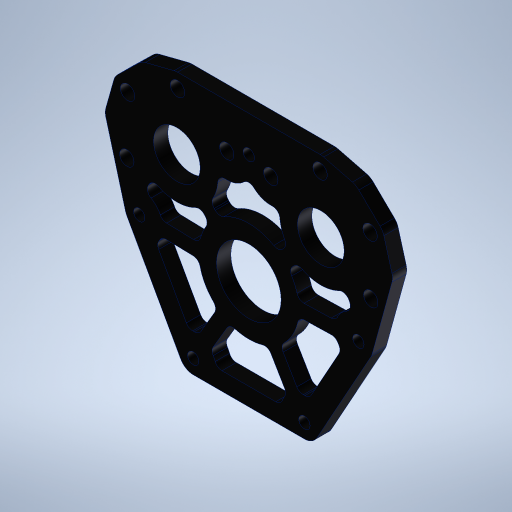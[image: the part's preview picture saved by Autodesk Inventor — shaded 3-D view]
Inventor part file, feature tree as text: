
AUTODESK INVENTOR PART (.ipt)
format: ipt  version: 2024 (Build 280153000, 153)  size: 578,560 bytes
history: native  units: in
note: dims shown in document units (in); Inventor stores cm internally (conversion verified against a paired STEP export)
features: fillet x6, extrude x2, sketch x2, projected_geometry x1
ambient origin geometry x8: Origin, YZ Plane, XZ Plane, XY Plane, X Axis, Y Axis, Z Axis, Center Point
bodies: Solid1 (feature_tree)
feature tree (11):
  extrude  "Extrusion1"  Depth=0.1in
  extrude  "Extrusion2"  Depth=0.125in
  fillet  "Fillet1"  Radius=2.0in
  fillet  "Fillet2"  Radius=0.6in
  fillet  "Fillet3"  Radius=0.25in
  fillet  "Fillet4"  Radius=4.7244in
  fillet  "Fillet5"  Radius=0.5in
  fillet  "Fillet6"  Radius=0.196in
  sketch  "Sketch1"  dims[d0=3.0in d1=0.1in]
  sketch  "Sketch2"  dims[d2=1.125in d3=2.367in d4=2.0in d5=0.6in d6=0.25in d7=4.7244in d9=360.0deg d12=0.5in d14=0.196in d15=0.313in d16=0.063in d17=0.6in d18=0.8125in d19=0.8125in d20=0.5in d21=0.5in d22=0.5in d23=0.5in d24=0.5in d25=0.5in d26=0.5in d27=0.5in d28=0.5in d29=0.5in d30=0.25in d31=0.0in d32=0.1875in d33=0.1875in d34=0.1875in d35=0.1875in d36=0.1875in d37=0.125in d38=0.125in d39=0.125in d40=0.125in d41=0.125in d42=0.125in d43=0.125in d44=0.125in d45=0.125in d46=0.125in d47=0.125in d48=0.125in d49=0.125in d50=0.125in d51=0.125in d52=0.125in d53=0.125in d54=0.125in d55=0.125in d56=0.125in d57=0.125in d58=0.125in d59=0.125in d60=0.125in d61=0.125in d62=0.125in d63=0.125in d64=0.125in d65=0.125in d66=0.125in d67=0.125in d68=1.0in d69=0.0in d70=0.125in d71=0.125in d72=0.125in d73=0.125in d74=0.125in d75=0.125in d76=0.125in d77=0.125in d78=0.125in d79=0.125in]
  projected_geometry  "Projected Loop1"
